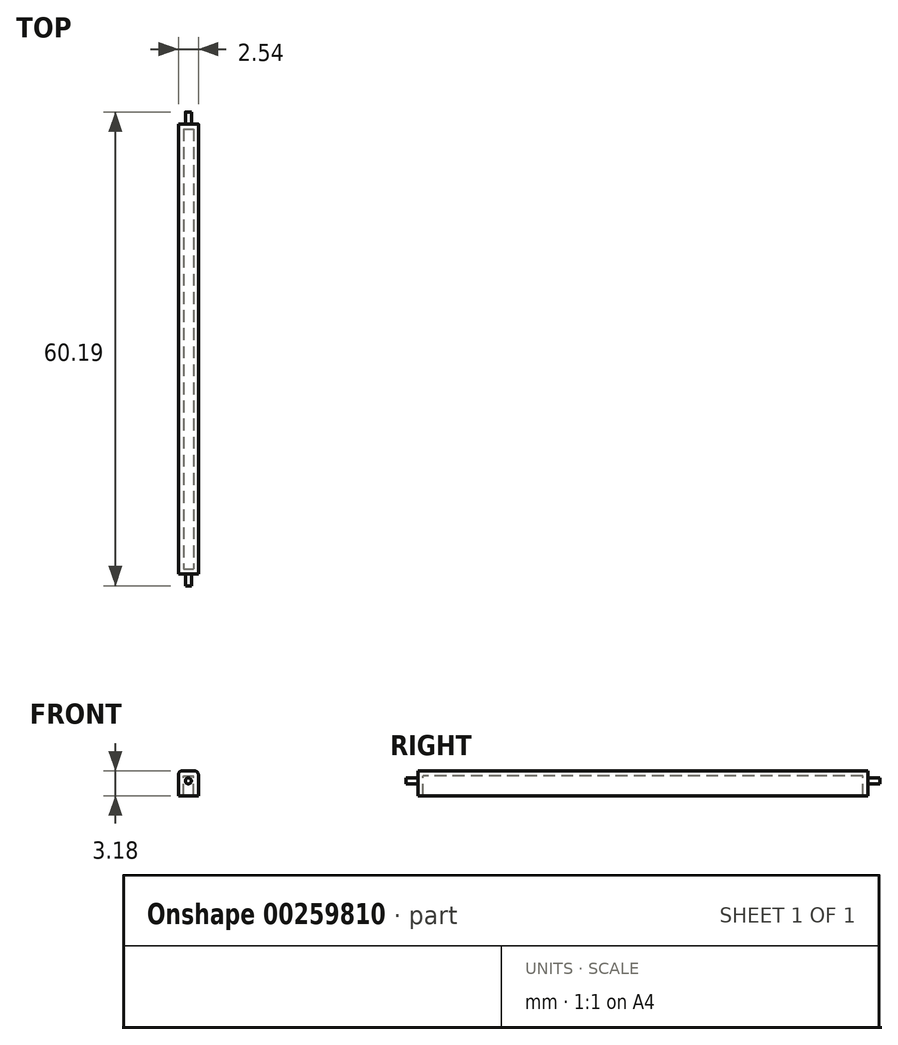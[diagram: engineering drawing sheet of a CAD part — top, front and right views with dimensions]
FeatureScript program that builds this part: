
annotation { "Feature Type Name" : "Feature", "Feature Type Description" : "" }
export const myFeature = defineFeature(function(context is Context, id is Id, definition is map)
    precondition{}
    {
        {
            var Q0;
            Q0=qCreatedBy(makeId("Front.planeOp"),FACE);
            var sketch = newSketch(context, id + "F0", { "sketchPlane" : qUnion([Q0])});
            skLineSegment(sketch, "E0.bottom", {"start": v(-1.27, 0) * mm, "end": v(1.27, 0) * mm});
            skLineSegment(sketch, "E0.top", {"start": v(-0.76, 3.17) * mm, "end": v(0.76, 3.17) * mm});
            skLineSegment(sketch, "E0.left", {"start": v(-1.27, 0) * mm, "end": v(-1.27, 2.67) * mm});
            skLineSegment(sketch, "E0.right", {"start": v(1.27, 0) * mm, "end": v(1.27, 2.67) * mm});
            skPoint(sketch, "E1.visualSharp", {"position": v(-1.27, 3.17) * mm});
            skArc(sketch, "E1.filletArc", {"start": v(-0.76, 3.18) * mm, "mid": v(-1.12, 3.03) * mm, "end": v(-1.27, 2.67) * mm});
            skPoint(sketch, "E2.visualSharp", {"position": v(1.27, 3.17) * mm});
            skArc(sketch, "E2.filletArc", {"start": v(1.27, 2.67) * mm, "mid": v(1.12, 3.03) * mm, "end": v(0.76, 3.18) * mm});
            skSolve(sketch);
        }
        {
            var Q0;
            Q0 = qSketchRegion(id + "F0", true);
            extrude(context, id + "F1", {"entities" : qUnion([Q0]), "oppositeDirection" : true, "depth" : 57.15 * mm});
        }
        {
            var Q0;
            Q0=makeQuery(id+"F1.opExtrude","CAP_FACE",FACE,{"disambiguationData":[OSD([sQuery(id+"F0.wireOp",EDGE,"E0.bottom"),sQuery(id+"F0.wireOp",EDGE,"E0.top"),sQuery(id+"F0.wireOp",EDGE,"E0.left"),sQuery(id+"F0.wireOp",EDGE,"E0.right"),sQuery(id+"F0.wireOp",EDGE,"E1.filletArc"),sQuery(id+"F0.wireOp",EDGE,"E2.filletArc")])],"isStart":true});
            var sketch = newSketch(context, id + "F2", { "sketchPlane" : qUnion([Q0])});
            skCircle(sketch, "E3", {"center": v(0, 1.9) * mm, "radius": 0.38 * mm});
            skSolve(sketch);
        }
        {
            var Q0;
            Q0 = qSketchRegion(id + "F2", true);
            extrude(context, id + "F3", {"entities" : qUnion([Q0]), "operationType" : NewBodyOperationType.ADD, "depth" : 1.52 * mm});
        }
        {
            var Q0;
            Q0=makeQuery(id+"F1.opExtrude","CAP_FACE",FACE,{"disambiguationData":[OSD([sQuery(id+"F0.wireOp",EDGE,"E0.bottom"),sQuery(id+"F0.wireOp",EDGE,"E0.top"),sQuery(id+"F0.wireOp",EDGE,"E0.left"),sQuery(id+"F0.wireOp",EDGE,"E0.right"),sQuery(id+"F0.wireOp",EDGE,"E1.filletArc"),sQuery(id+"F0.wireOp",EDGE,"E2.filletArc")])],"isStart":false});
            var sketch = newSketch(context, id + "F4", { "sketchPlane" : qUnion([Q0])});
            skCircle(sketch, "E4", {"center": v(0, 1.9) * mm, "radius": 0.38 * mm});
            skSolve(sketch);
        }
        {
            var Q0;
            Q0 = qSketchRegion(id + "F4", true);
            extrude(context, id + "F5", {"entities" : qUnion([Q0]), "operationType" : NewBodyOperationType.ADD, "depth" : 1.52 * mm});
        }
        {
            var Q0;
            Q0=makeQuery(id+"F1.opExtrude","SWEPT_FACE",FACE,{"disambiguationData":[OSD([sQuery(id+"F0.wireOp",EDGE,"E0.bottom")])]});
            shell(context, id + "F6", {"entities" : qUnion([Q0]), "thickness" : 0.64 * mm});
        }
    });
